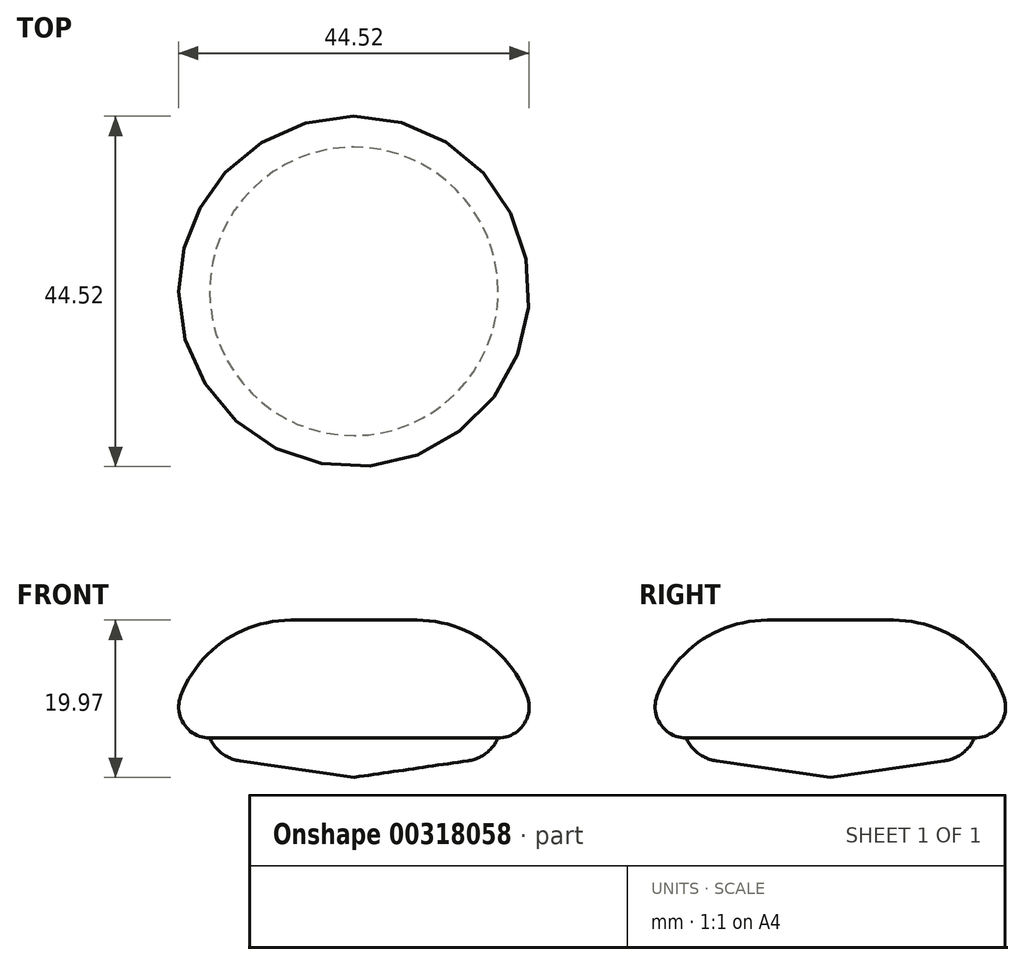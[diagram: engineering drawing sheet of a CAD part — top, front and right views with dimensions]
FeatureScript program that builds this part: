
annotation { "Feature Type Name" : "Feature", "Feature Type Description" : "" }
export const myFeature = defineFeature(function(context is Context, id is Id, definition is map)
    precondition{}
    {
        {
            var Q0;
            Q0=qCreatedBy(makeId("Front.planeOp"),FACE);
            var sketch = newSketch(context, id + "F0", { "sketchPlane" : qUnion([Q0])});
            skLineSegment(sketch, "E0", {"start": v(0, 0) * mm, "end": v(8, 0) * mm});
            skArc(sketch, "E1", {"start": v(22, -9.61) * mm, "mid": v(16.5, -2.64) * mm, "end": v(8, 0) * mm});
            skArc(sketch, "E2", {"start": v(18.32, -14.97) * mm, "mid": v(21.57, -13.26) * mm, "end": v(22, -9.61) * mm});
            skLineSegment(sketch, "E3", {"start": v(18.32, -14.97) * mm, "end": v(0, -14.97) * mm, "construction": true});
            skArc(sketch, "E4", {"start": v(14.48, -17.87) * mm, "mid": v(16.77, -16.92) * mm, "end": v(18.32, -14.97) * mm});
            skLineSegment(sketch, "E5", {"start": v(14.48, -17.87) * mm, "end": v(0, -19.97) * mm});
            skLineSegment(sketch, "E6", {"start": v(0, -19.97) * mm, "end": v(0, 0) * mm});
            skSolve(sketch);
        }
        {
            var Q0;
            Q0=makeQuery(id+"F0.imprint","IMPRINT",FACE,{"disambiguationData":[TD([[makeQuery(id+"F0.imprint","IMPRINT",EDGE,{"derivedFrom":sQuery(id+"F0.wireOp",EDGE,"E0")}),-1.0]])]});
            var Q1;
            Q1=sQuery(id+"F0.wireOp",EDGE,"E6");
            revolve(context, id + "F1", {"entities" : qUnion([Q0]), "axis" : qUnion([Q1]), "revolveType" : RevolveType.FULL});
        }
    });
